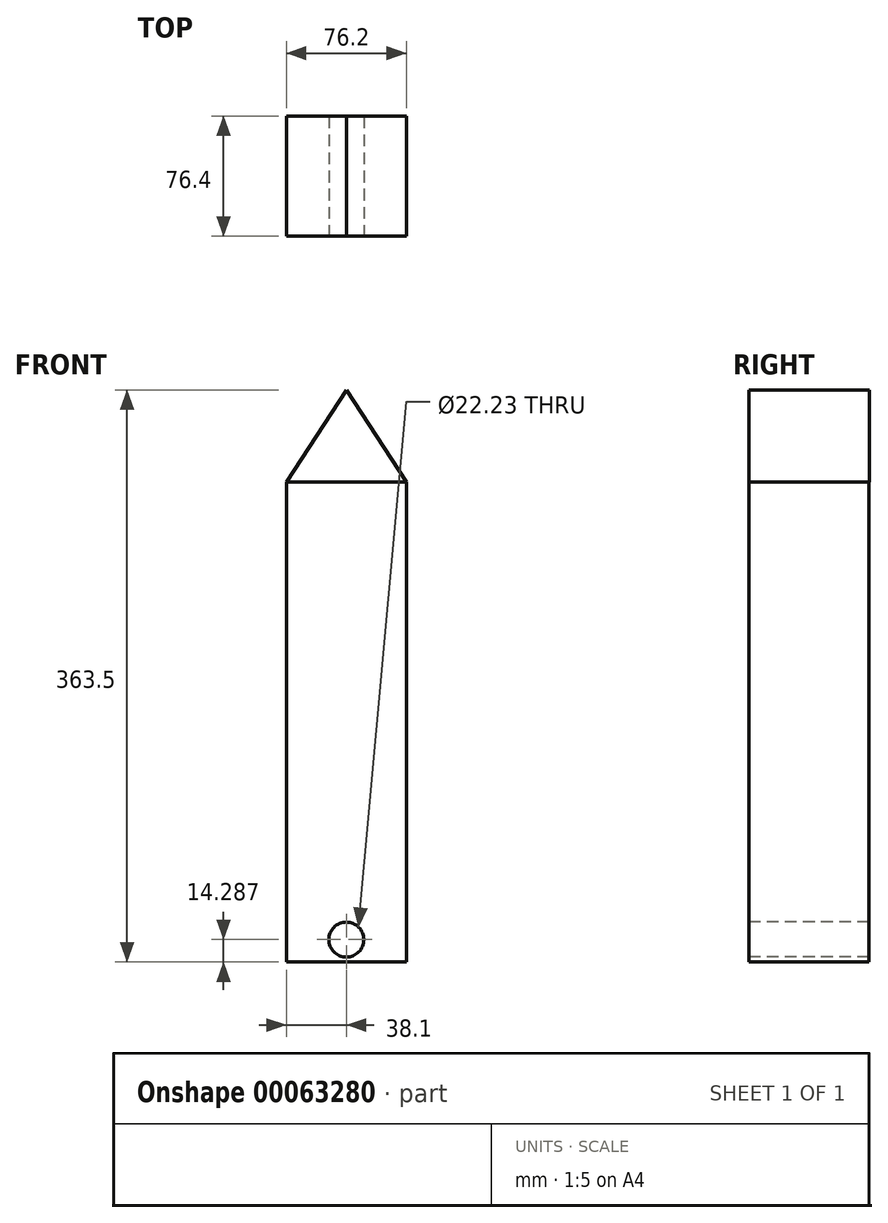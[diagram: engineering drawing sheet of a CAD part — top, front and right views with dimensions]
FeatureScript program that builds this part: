
annotation { "Feature Type Name" : "Feature", "Feature Type Description" : "" }
export const myFeature = defineFeature(function(context is Context, id is Id, definition is map)
    precondition{}
    {
        {
            var Q0;
            Q0=qCreatedBy(makeId("Top.planeOp"),FACE);
            var sketch = newSketch(context, id + "F0", { "sketchPlane" : qUnion([Q0])});
            skLineSegment(sketch, "E0.rect.bottom", {"start": v(38.1, -38.1) * mm, "end": v(-38.1, -38.1) * mm});
            skLineSegment(sketch, "E0.rect.top", {"start": v(38.1, 38.1) * mm, "end": v(-38.1, 38.1) * mm});
            skLineSegment(sketch, "E0.rect.left", {"start": v(38.1, -38.1) * mm, "end": v(38.1, 38.1) * mm});
            skLineSegment(sketch, "E0.rect.right", {"start": v(-38.1, -38.1) * mm, "end": v(-38.1, 38.1) * mm});
            skPoint(sketch, "E0.rect.middle", {"position": v(0, 0) * mm});
            skSolve(sketch);
        }
        {
            var Q0;
            Q0 = qSketchRegion(id + "F0", true);
            extrude(context, id + "F1", {"entities" : qUnion([Q0]), "depth" : 304.8 * mm});
        }
        {
            var Q0;
            Q0=makeQuery(id+"F1.opExtrude","SWEPT_FACE",FACE,{"disambiguationData":[OSD([sQuery(id+"F0.wireOp",EDGE,"E0.rect.bottom")])]});
            var sketch = newSketch(context, id + "F2", { "sketchPlane" : qUnion([Q0])});
            skLineSegment(sketch, "E1", {"start": v(-38.1, 304.8) * mm, "end": v(0, 363.5) * mm});
            skLineSegment(sketch, "E2", {"start": v(0, 363.5) * mm, "end": v(38.1, 304.8) * mm});
            skLineSegment(sketch, "E3", {"start": v(38.1, 304.8) * mm, "end": v(-38.1, 304.8) * mm});
            skSolve(sketch);
        }
        {
            var Q0;
            Q0 = qSketchRegion(id + "F2", true);
            extrude(context, id + "F3", {"entities" : qUnion([Q0]), "oppositeDirection" : true, "depth" : 76.4 * mm});
        }
        {
            var Q0;
            Q0=makeQuery(id+"F1.opExtrude","SWEPT_FACE",FACE,{"disambiguationData":[OSD([sQuery(id+"F0.wireOp",EDGE,"E0.rect.bottom")])]});
            var sketch = newSketch(context, id + "F4", { "sketchPlane" : qUnion([Q0])});
            skCircle(sketch, "E4", {"center": v(0, 14.29) * mm, "radius": 11.11 * mm});
            skSolve(sketch);
        }
        {
            var Q0;
            Q0 = qSketchRegion(id + "F4", true);
            extrude(context, id + "F5", {"entities" : qUnion([Q0]), "operationType" : NewBodyOperationType.REMOVE, "oppositeDirection" : true, "depth" : 286.6 * mm});
        }
    });
